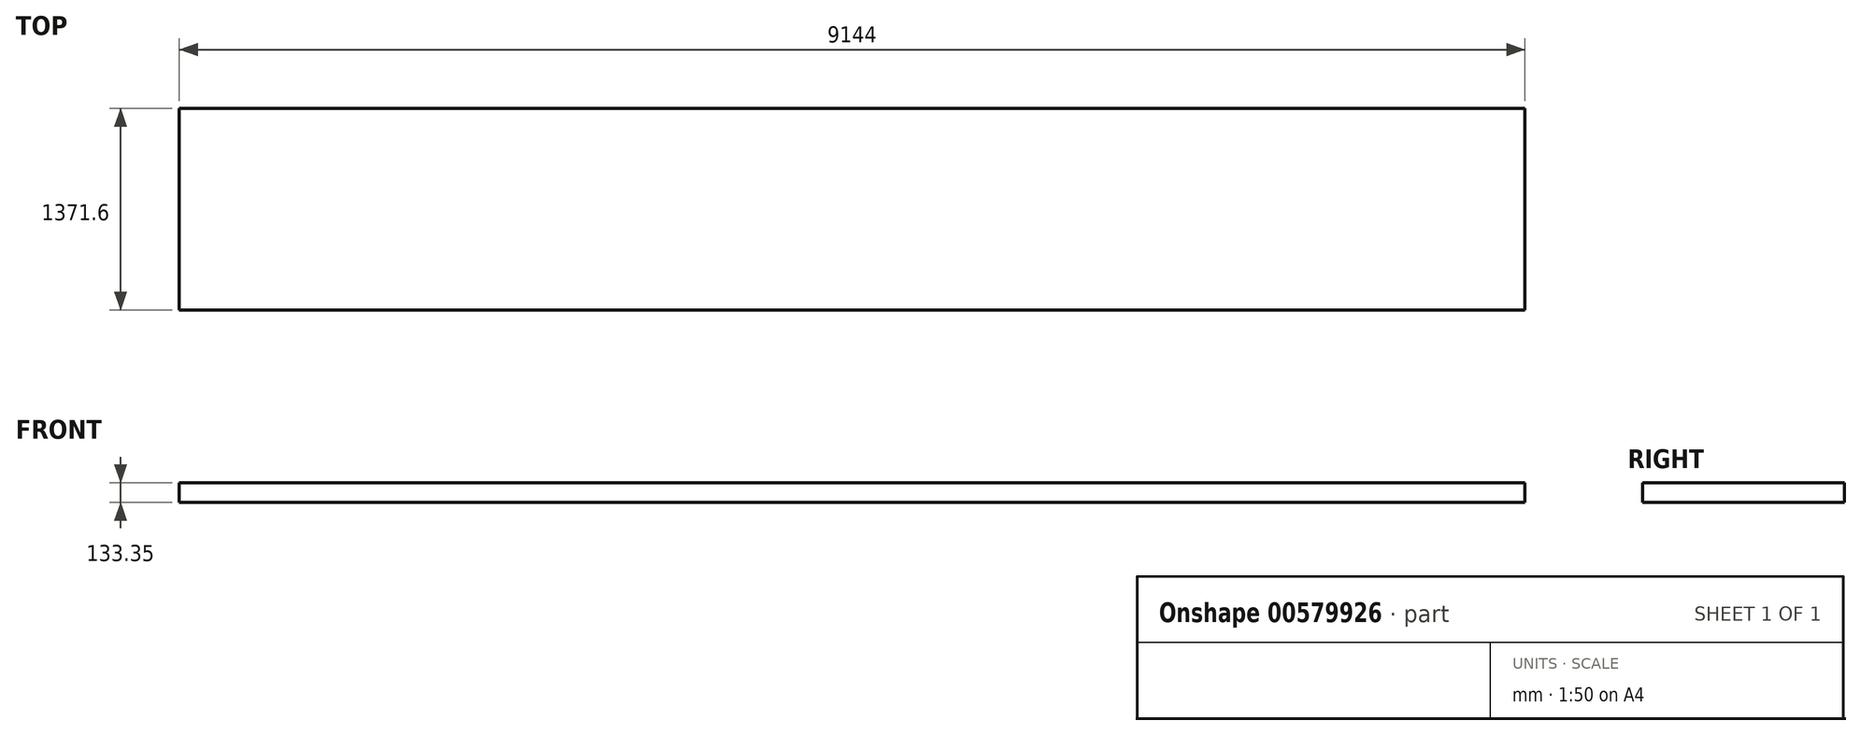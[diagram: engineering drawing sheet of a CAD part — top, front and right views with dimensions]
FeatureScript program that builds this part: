
annotation { "Feature Type Name" : "Feature", "Feature Type Description" : "" }
export const myFeature = defineFeature(function(context is Context, id is Id, definition is map)
    precondition{}
    {
        {
            var Q0;
            Q0=qCreatedBy(makeId("Top.planeOp"),FACE);
            var sketch = newSketch(context, id + "F0", { "sketchPlane" : qUnion([Q0])});
            skLineSegment(sketch, "E0.bottom", {"start": v(-4617.66, -1595.17) * mm, "end": v(4526.34, -1595.17) * mm});
            skLineSegment(sketch, "E0.top", {"start": v(-4617.66, -2966.77) * mm, "end": v(4526.34, -2966.77) * mm});
            skLineSegment(sketch, "E0.left", {"start": v(-4617.66, -1595.17) * mm, "end": v(-4617.66, -2966.77) * mm});
            skLineSegment(sketch, "E0.right", {"start": v(4526.34, -1595.17) * mm, "end": v(4526.34, -2966.77) * mm});
            skSolve(sketch);
        }
        {
            var Q0;
            Q0=makeQuery(id+"F0.imprint","IMPRINT",FACE,{"disambiguationData":[TD([[makeQuery(id+"F0.imprint","IMPRINT",EDGE,{"derivedFrom":sQuery(id+"F0.wireOp",EDGE,"E0.bottom")}),-1.0]])]});
            extrude(context, id + "F1", {"entities" : qUnion([Q0]), "depth" : 133.35 * mm, "offsetDistance" : 25.4 * mm});
        }
    });
